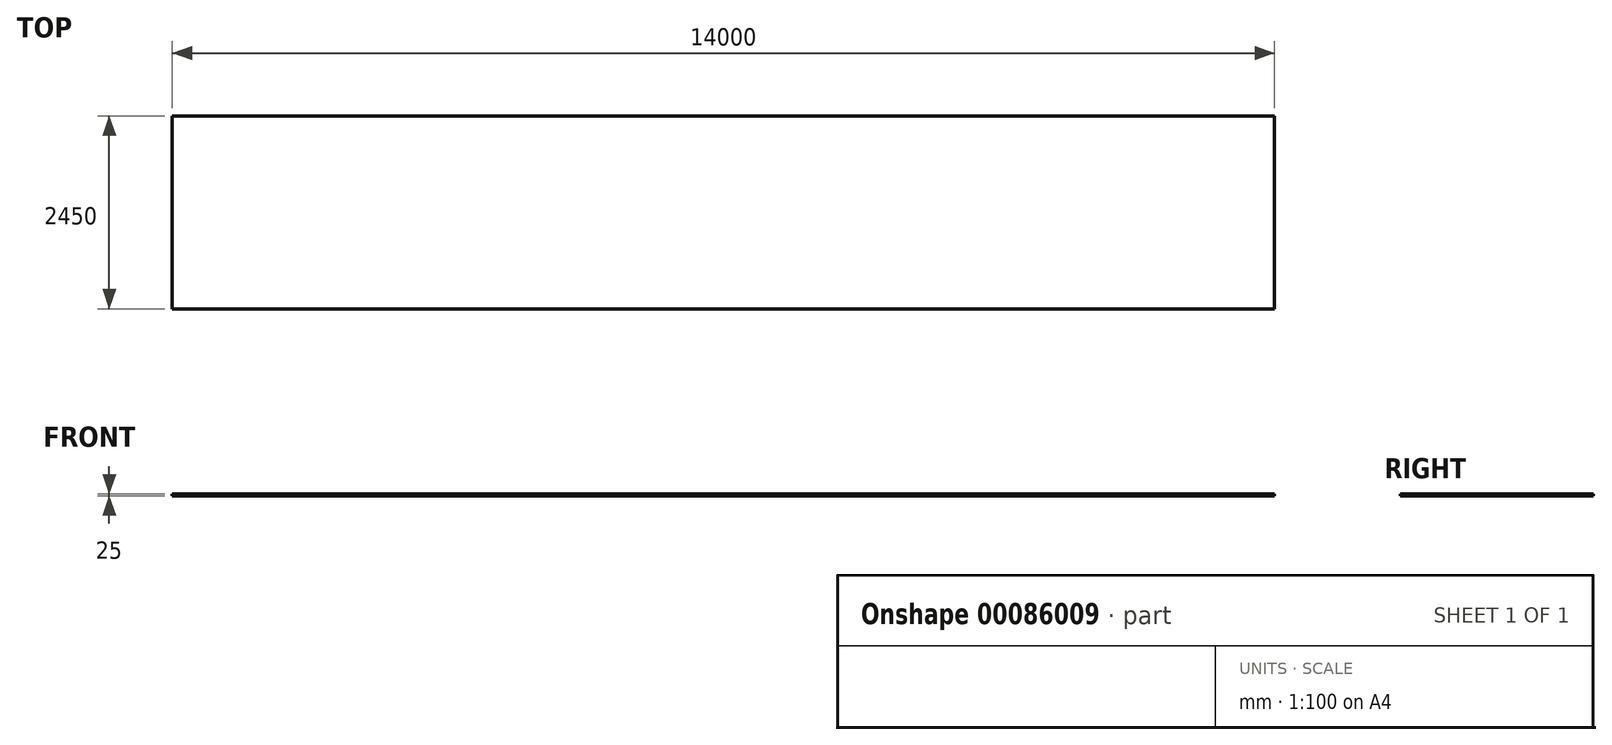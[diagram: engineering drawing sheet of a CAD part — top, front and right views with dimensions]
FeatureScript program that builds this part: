
annotation { "Feature Type Name" : "Feature", "Feature Type Description" : "" }
export const myFeature = defineFeature(function(context is Context, id is Id, definition is map)
    precondition{}
    {
        {
            var Q0;
            Q0=qCreatedBy(makeId("Top.planeOp"),FACE);
            var sketch = newSketch(context, id + "F0", { "sketchPlane" : qUnion([Q0])});
            skLineSegment(sketch, "E0.bottom", {"start": v(7000, 1225) * mm, "end": v(-7000, 1225) * mm});
            skLineSegment(sketch, "E0.top", {"start": v(7000, -1225) * mm, "end": v(-7000, -1225) * mm});
            skLineSegment(sketch, "E0.left", {"start": v(7000, 1225) * mm, "end": v(7000, -1225) * mm});
            skLineSegment(sketch, "E0.right", {"start": v(-7000, 1225) * mm, "end": v(-7000, -1225) * mm});
            skPoint(sketch, "E0.middle", {"position": v(0, 0) * mm});
            skSolve(sketch);
        }
        {
            var Q0;
            Q0=makeQuery(id+"F0.imprint","IMPRINT",FACE,{"disambiguationData":[TD([[makeQuery(id+"F0.imprint","IMPRINT",EDGE,{"derivedFrom":sQuery(id+"F0.wireOp",EDGE,"E0.bottom")}),1.0]])]});
            extrude(context, id + "F1", {"entities" : qUnion([Q0]), "depth" : 25 * mm});
        }
    });
